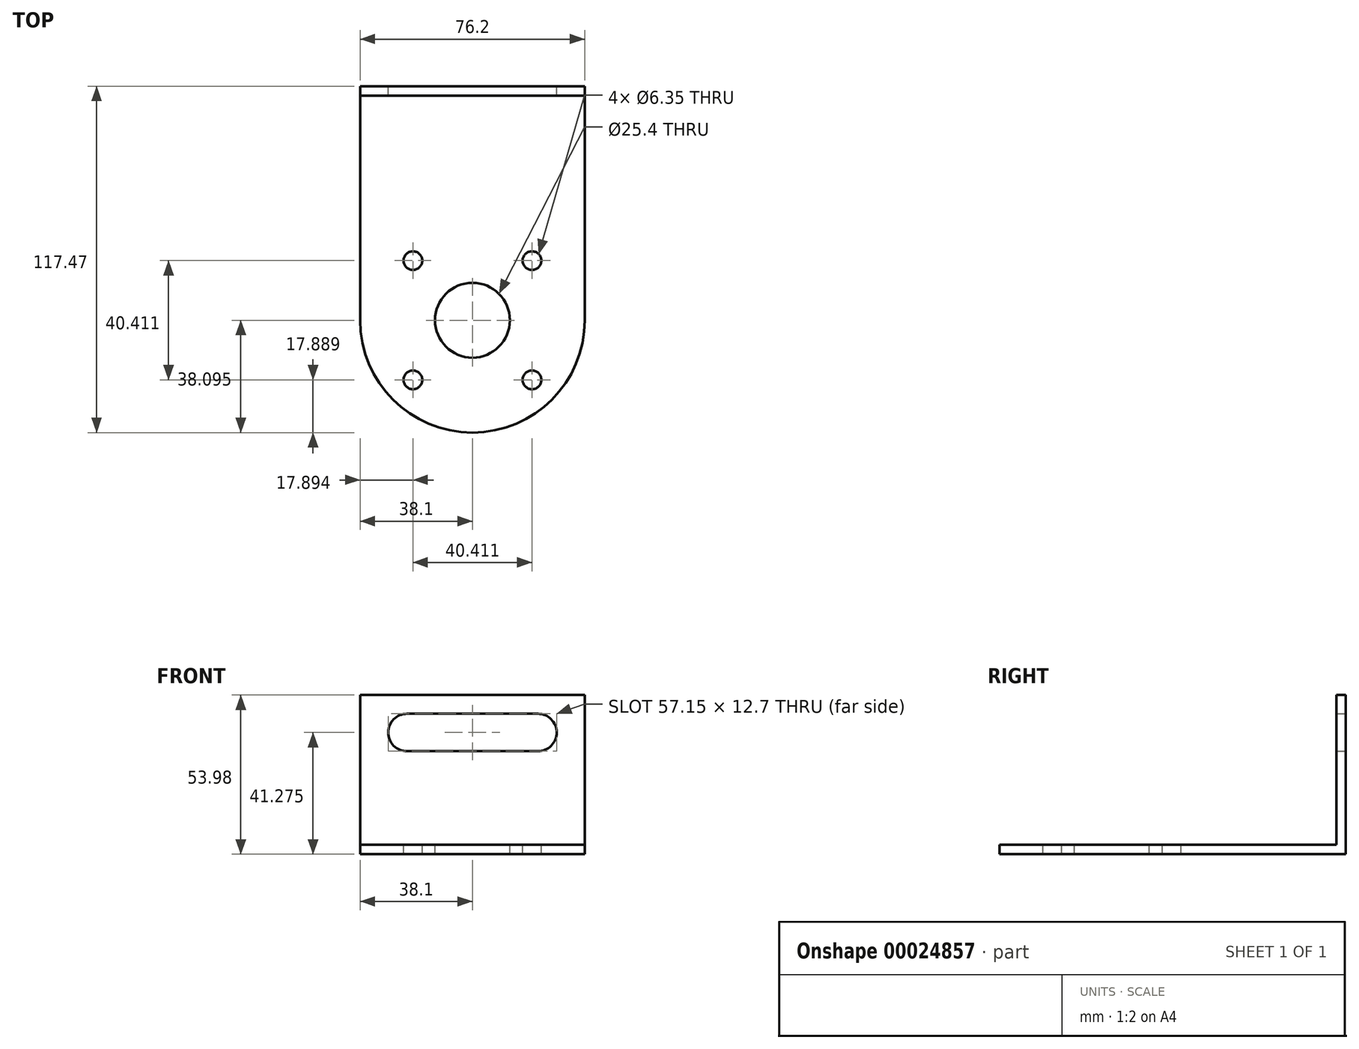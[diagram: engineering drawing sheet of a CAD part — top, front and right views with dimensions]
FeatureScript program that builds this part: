
annotation { "Feature Type Name" : "Feature", "Feature Type Description" : "" }
export const myFeature = defineFeature(function(context is Context, id is Id, definition is map)
    precondition{}
    {
        {
            var Q0;
            Q0=qCreatedBy(makeId("Front.planeOp"),FACE);
            var sketch = newSketch(context, id + "F0", { "sketchPlane" : qUnion([Q0])});
            skLineSegment(sketch, "E0", {"start": v(0, 0) * mm, "end": v(0, 53.98) * mm});
            skLineSegment(sketch, "E1", {"start": v(0, 53.98) * mm, "end": v(76.2, 53.98) * mm});
            skLineSegment(sketch, "E2", {"start": v(76.2, 53.98) * mm, "end": v(76.2, 0) * mm});
            skLineSegment(sketch, "E3", {"start": v(0, 0) * mm, "end": v(76.2, 0) * mm});
            skLineSegment(sketch, "E4", {"start": v(0, 41.27) * mm, "end": v(76.2, 41.27) * mm, "construction": true});
            skLineSegment(sketch, "E5", {"start": v(15.88, 53.98) * mm, "end": v(15.88, 0) * mm, "construction": true});
            skLineSegment(sketch, "E6", {"start": v(60.33, 53.98) * mm, "end": v(60.33, 0) * mm, "construction": true});
            skArc(sketch, "E7", {"start": v(15.88, 47.62) * mm, "mid": v(9.52, 41.27) * mm, "end": v(15.88, 34.92) * mm});
            skArc(sketch, "E8", {"start": v(60.33, 34.92) * mm, "mid": v(66.68, 41.27) * mm, "end": v(60.33, 47.62) * mm});
            skLineSegment(sketch, "E9", {"start": v(15.88, 47.62) * mm, "end": v(60.33, 47.62) * mm});
            skLineSegment(sketch, "E10", {"start": v(15.88, 34.92) * mm, "end": v(60.33, 34.92) * mm});
            skSolve(sketch);
        }
        {
            var Q0;
            Q0=makeQuery(id+"F0.imprint","IMPRINT",FACE,{"disambiguationData":[TD([[makeQuery(id+"F0.imprint","IMPRINT",EDGE,{"derivedFrom":sQuery(id+"F0.wireOp",EDGE,"E0")}),-1.0]])]});
            extrude(context, id + "F1", {"entities" : qUnion([Q0]), "depth" : 3.17 * mm});
        }
        {
            var Q0;
            Q0=makeQuery(id+"F1.opExtrude","CAP_FACE",FACE,{"disambiguationData":[OSD([sQuery(id+"F0.wireOp",EDGE,"E0"),sQuery(id+"F0.wireOp",EDGE,"E1"),sQuery(id+"F0.wireOp",EDGE,"E2"),sQuery(id+"F0.wireOp",EDGE,"E3"),sQuery(id+"F0.wireOp",EDGE,"E7"),sQuery(id+"F0.wireOp",EDGE,"E8"),sQuery(id+"F0.wireOp",EDGE,"E9"),sQuery(id+"F0.wireOp",EDGE,"E10")])],"isStart":false});
            var sketch = newSketch(context, id + "F2", { "sketchPlane" : qUnion([Q0])});
            skLineSegment(sketch, "E11", {"start": v(0, 3.18) * mm, "end": v(76.2, 3.18) * mm});
            skSolve(sketch);
        }
        {
            var Q0;
            {var subQ1=sQuery(id+"F2.wireOp",EDGE,"E11");Q0=makeQuery(id+"F2.imprint","IMPRINT",FACE,{"disambiguationData":[TD([[makeQuery(id+"F2.imprint","IMPRINT",EDGE,{"derivedFrom":subQ1}),-1.0]])]});}
            extrude(context, id + "F3", {"entities" : qUnion([Q0]), "operationType" : NewBodyOperationType.ADD, "depth" : 76.2 * mm});
        }
        {
            var Q0;
            Q0=makeQuery(id+"F3.opExtrude","SWEPT_FACE",FACE,{"disambiguationData":[OSD([sQuery(id+"F2.wireOp",EDGE,"E11")])]});
            var sketch = newSketch(context, id + "F4", { "sketchPlane" : qUnion([Q0])});
            skArc(sketch, "E12", {"start": v(0, -79.38) * mm, "mid": v(38.1, -117.47) * mm, "end": v(76.2, -79.38) * mm});
            skLineSegment(sketch, "E13", {"start": v(0, -79.38) * mm, "end": v(76.2, -79.38) * mm});
            skSolve(sketch);
        }
        {
            var Q0;
            Q0=makeQuery(id+"F4.imprint","IMPRINT",FACE,{"disambiguationData":[TD([[makeQuery(id+"F4.imprint","IMPRINT",EDGE,{"derivedFrom":sQuery(id+"F4.wireOp",EDGE,"E12")}),1.0]])]});
            extrude(context, id + "F5", {"entities" : qUnion([Q0]), "operationType" : NewBodyOperationType.ADD, "oppositeDirection" : true, "depth" : 3.17 * mm});
        }
        {
            var Q0;
            Q0=makeQuery(id+"F5.boolean.opBoolean","MERGE",FACE,{"derivedFrom":[makeQuery(id+"F3.opExtrude","SWEPT_FACE",FACE,{"disambiguationData":[OSD([sQuery(id+"F2.wireOp",EDGE,"E11")])]}),makeQuery(id+"F5.opExtrude","CAP_FACE",FACE,{"disambiguationData":[OSD([sQuery(id+"F4.wireOp",EDGE,"E12"),sQuery(id+"F4.wireOp",EDGE,"E13")])],"isStart":true})]});
            var sketch = newSketch(context, id + "F6", { "sketchPlane" : qUnion([Q0])});
            skLineSegment(sketch, "E14", {"start": v(0, -79.38) * mm, "end": v(76.2, -79.38) * mm, "construction": true});
            skLineSegment(sketch, "E15", {"start": v(38.1, -79.38) * mm, "end": v(38.1, -224.88) * mm, "construction": true});
            skCircle(sketch, "E16", {"center": v(38.1, -79.38) * mm, "radius": 12.7 * mm});
            skCircle(sketch, "E17", {"center": v(38.1, -79.38) * mm, "radius": 28.58 * mm, "construction": true});
            skLineSegment(sketch, "E18", {"start": v(38.1, -79.38) * mm, "end": v(60.55, -101.83) * mm, "construction": true});
            skCircle(sketch, "E19", {"center": v(58.3, -99.58) * mm, "radius": 3.18 * mm});
            skCircle(sketch, "E20.1.0", {"center": v(58.3, -59.17) * mm, "radius": 3.18 * mm});
            skCircle(sketch, "E20.2.0", {"center": v(17.9, -59.17) * mm, "radius": 3.18 * mm});
            skCircle(sketch, "E20.3.0", {"center": v(17.9, -99.58) * mm, "radius": 3.18 * mm});
            skSolve(sketch);
        }
        {
            var Q0;
            Q0=makeQuery(id+"F6.imprint","IMPRINT",FACE,{"disambiguationData":[TD([[makeQuery(id+"F6.imprint","IMPRINT",EDGE,{"derivedFrom":sQuery(id+"F6.wireOp",EDGE,"E16")}),1.0]])]});
            var Q1;
            Q1=makeQuery(id+"F6.imprint","IMPRINT",FACE,{"disambiguationData":[TD([[makeQuery(id+"F6.imprint","IMPRINT",EDGE,{"derivedFrom":sQuery(id+"F6.wireOp",EDGE,"E19")}),1.0]])]});
            var Q2;
            Q2=makeQuery(id+"F6.imprint","IMPRINT",FACE,{"disambiguationData":[TD([[makeQuery(id+"F6.imprint","IMPRINT",EDGE,{"derivedFrom":sQuery(id+"F6.wireOp",EDGE,"E20.1.0")}),1.0]])]});
            var Q3;
            Q3=makeQuery(id+"F6.imprint","IMPRINT",FACE,{"disambiguationData":[TD([[makeQuery(id+"F6.imprint","IMPRINT",EDGE,{"derivedFrom":sQuery(id+"F6.wireOp",EDGE,"E20.3.0")}),1.0]])]});
            var Q4;
            Q4=makeQuery(id+"F6.imprint","IMPRINT",FACE,{"disambiguationData":[TD([[makeQuery(id+"F6.imprint","IMPRINT",EDGE,{"derivedFrom":sQuery(id+"F6.wireOp",EDGE,"E20.2.0")}),1.0]])]});
            extrude(context, id + "F7", {"entities" : qUnion([Q0, Q1, Q2, Q3, Q4]), "operationType" : NewBodyOperationType.REMOVE, "oppositeDirection" : true, "depth" : 25.4 * mm});
        }
    });
